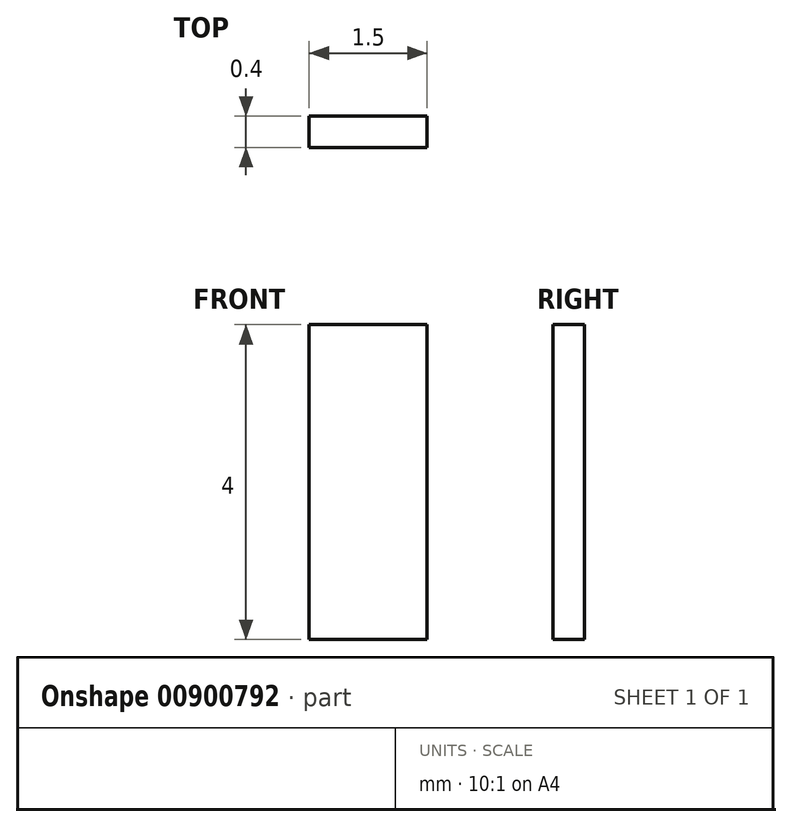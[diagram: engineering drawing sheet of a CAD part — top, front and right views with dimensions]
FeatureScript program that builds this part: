
annotation { "Feature Type Name" : "Feature", "Feature Type Description" : "" }
export const myFeature = defineFeature(function(context is Context, id is Id, definition is map)
    precondition{}
    {
        {
            var Q0;
            Q0=qCreatedBy(makeId("Front.planeOp"),FACE);
            var sketch = newSketch(context, id + "F0", { "sketchPlane" : qUnion([Q0])});
            skLineSegment(sketch, "E0", {"start": v(-1.55, 5.72) * mm, "end": v(-0.05, 5.72) * mm});
            skLineSegment(sketch, "E1", {"start": v(-0.05, 5.72) * mm, "end": v(-0.05, 1.72) * mm});
            skLineSegment(sketch, "E2", {"start": v(-0.05, 1.72) * mm, "end": v(-1.55, 1.72) * mm});
            skLineSegment(sketch, "E3", {"start": v(-1.55, 5.72) * mm, "end": v(-1.55, 1.72) * mm});
            skSolve(sketch);
        }
        {
            var Q0;
            Q0 = qSketchRegion(id + "F0", true);
            extrude(context, id + "F1", {"entities" : qUnion([Q0]), "depth" : 0.4 * mm, "offsetDistance" : 25 * mm});
        }
    });
